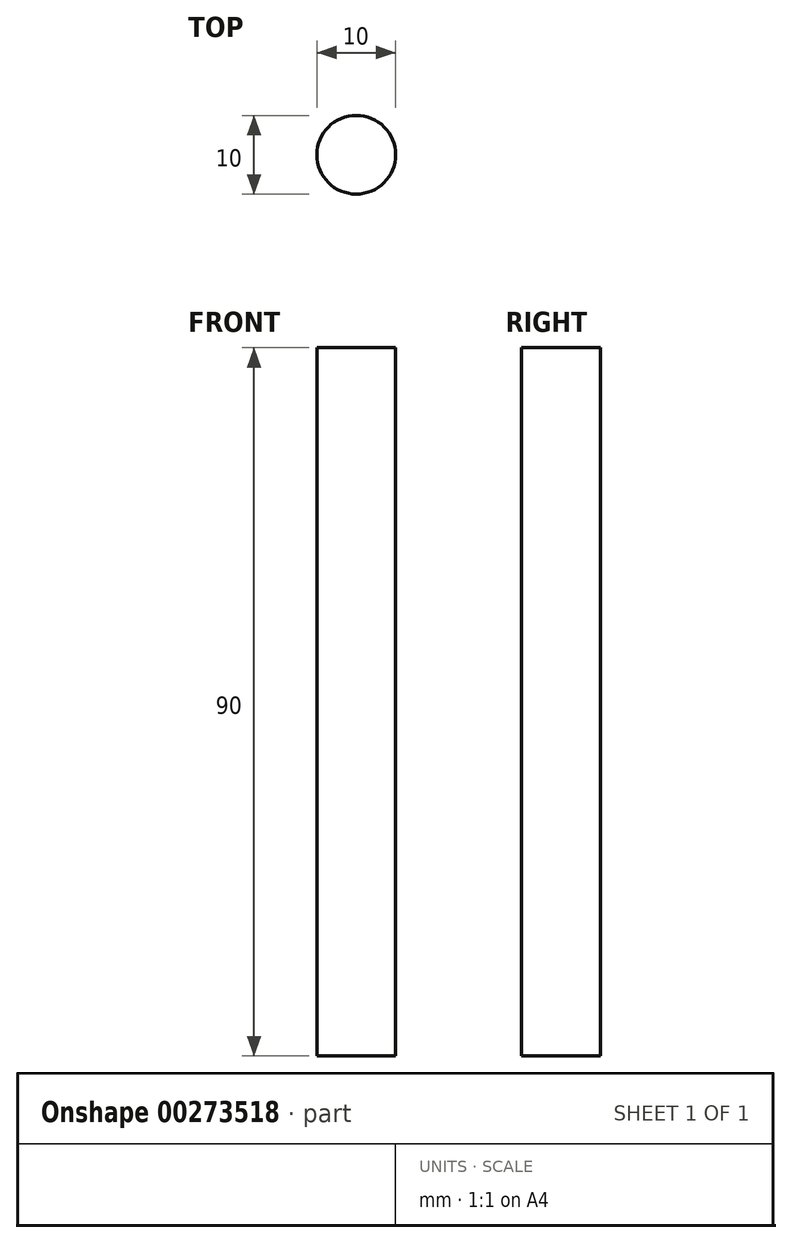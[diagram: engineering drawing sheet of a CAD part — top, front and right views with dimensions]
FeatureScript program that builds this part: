
annotation { "Feature Type Name" : "Feature", "Feature Type Description" : "" }
export const myFeature = defineFeature(function(context is Context, id is Id, definition is map)
    precondition{}
    {
        {
            var Q0;
            Q0=qCreatedBy(makeId("Top.planeOp"),FACE);
            var sketch = newSketch(context, id + "F0", { "sketchPlane" : qUnion([Q0])});
            skCircle(sketch, "E0", {"center": v(11.8, 14.1) * mm, "radius": 5 * mm});
            skSolve(sketch);
        }
        {
            var Q0;
            Q0 = qSketchRegion(id + "F0", true);
            extrude(context, id + "F1", {"entities" : qUnion([Q0]), "depth" : 90 * mm});
        }
    });
